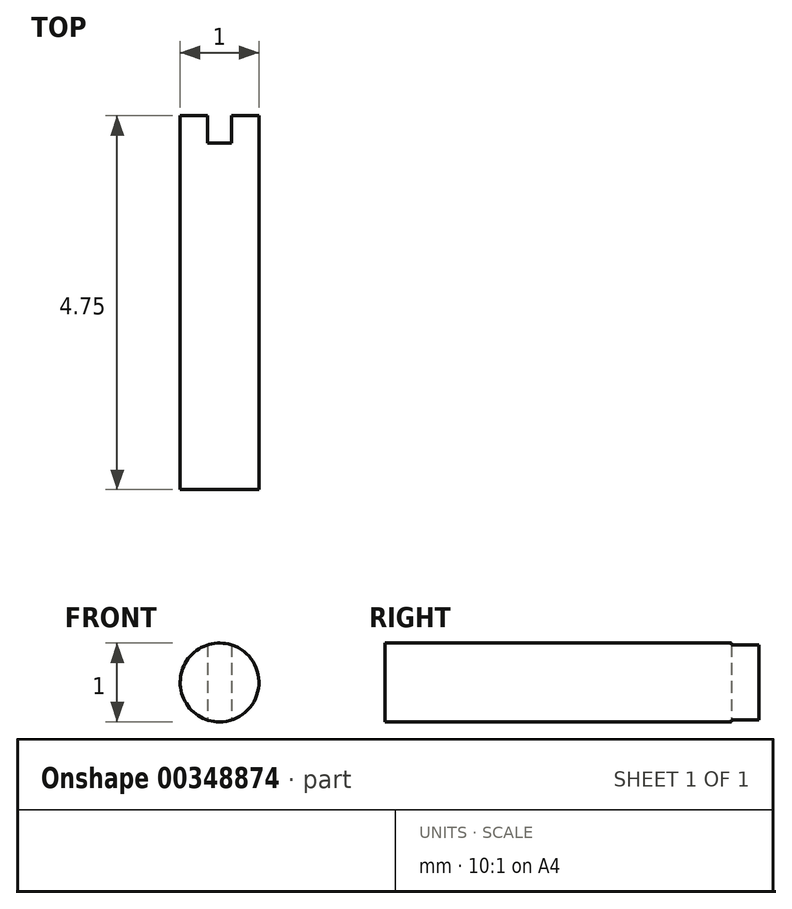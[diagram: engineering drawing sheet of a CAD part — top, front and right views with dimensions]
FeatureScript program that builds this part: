
annotation { "Feature Type Name" : "Feature", "Feature Type Description" : "" }
export const myFeature = defineFeature(function(context is Context, id is Id, definition is map)
    precondition{}
    {
        {
            var Q0;
            Q0=qCreatedBy(makeId("Front.planeOp"),FACE);
            var sketch = newSketch(context, id + "F0", { "sketchPlane" : qUnion([Q0])});
            skCircle(sketch, "E0", {"center": v(0, 0) * mm, "radius": 0.5 * mm});
            skSolve(sketch);
        }
        {
            var Q0;
            Q0=qSketchRegion(id+"F0",true);
            extrude(context, id + "F1", {"entities" : qUnion([Q0]), "depth" : 4.75 * mm});
        }
        {
            var Q0;
            Q0=qCreatedBy(makeId("Top.planeOp"),FACE);
            var sketch = newSketch(context, id + "F2", { "sketchPlane" : qUnion([Q0])});
            skLineSegment(sketch, "E1", {"start": v(0, 0) * mm, "end": v(0, -4.88) * mm, "construction": true});
            skLineSegment(sketch, "E2.bottom", {"start": v(-0.15, 0) * mm, "end": v(0.15, 0) * mm});
            skLineSegment(sketch, "E2.top", {"start": v(-0.15, -0.35) * mm, "end": v(0.15, -0.35) * mm});
            skLineSegment(sketch, "E2.left", {"start": v(-0.15, 0) * mm, "end": v(-0.15, -0.35) * mm});
            skLineSegment(sketch, "E2.right", {"start": v(0.15, 0) * mm, "end": v(0.15, -0.35) * mm});
            skSolve(sketch);
        }
        {
            var Q0;
            Q0=qSketchRegion(id+"F2",true);
            extrude(context, id + "F3", {"entities" : qUnion([Q0]), "operationType" : NewBodyOperationType.REMOVE, "endBound" : BoundingType.SYMMETRIC, "depth" : 25 * mm});
        }
    });
